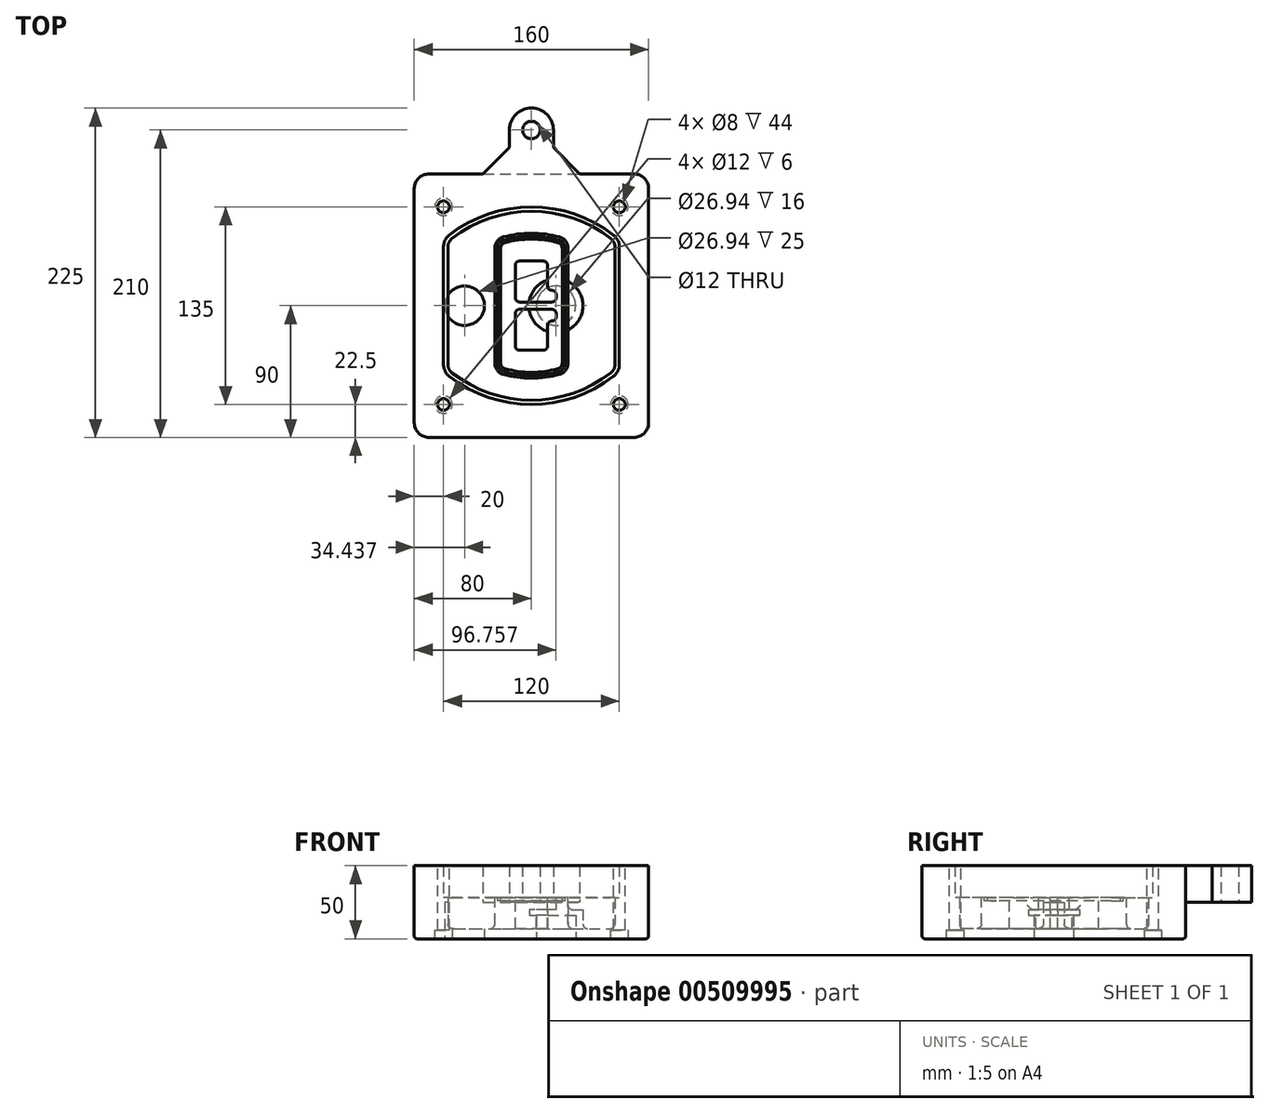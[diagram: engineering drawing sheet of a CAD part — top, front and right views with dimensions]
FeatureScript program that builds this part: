
annotation { "Feature Type Name" : "Feature", "Feature Type Description" : "" }
export const myFeature = defineFeature(function(context is Context, id is Id, definition is map)
    precondition{}
    {
        {
            var Q0;
            Q0=qCreatedBy(makeId("Top.planeOp"),FACE);
            var sketch = newSketch(context, id + "F0", { "sketchPlane" : qUnion([Q0])});
            skPoint(sketch, "E0.rect.middle", {"position": v(0, 0) * mm});
            skLineSegment(sketch, "E1.bottom", {"start": v(-70, -90) * mm, "end": v(70, -90) * mm});
            skLineSegment(sketch, "E1.top", {"start": v(-70, 90) * mm, "end": v(70, 90) * mm});
            skLineSegment(sketch, "E1.left", {"start": v(-80, -80) * mm, "end": v(-80, 80) * mm});
            skLineSegment(sketch, "E1.right", {"start": v(80, -80) * mm, "end": v(80, 80) * mm});
            skLineSegment(sketch, "E2", {"start": v(-80, 90) * mm, "end": v(80, -90) * mm, "construction": true});
            skLineSegment(sketch, "E3", {"start": v(80, 90) * mm, "end": v(-80, -90) * mm, "construction": true});
            skCircle(sketch, "E4", {"center": v(-60, 67.5) * mm, "radius": 4 * mm});
            skCircle(sketch, "E5", {"center": v(60, 67.5) * mm, "radius": 4 * mm});
            skCircle(sketch, "E6", {"center": v(60, -67.5) * mm, "radius": 4 * mm});
            skCircle(sketch, "E7", {"center": v(-60, -67.5) * mm, "radius": 4 * mm});
            skLineSegment(sketch, "E8", {"start": v(-60, 67.5) * mm, "end": v(60, 67.5) * mm, "construction": true});
            skLineSegment(sketch, "E9", {"start": v(60, 67.5) * mm, "end": v(60, -67.5) * mm, "construction": true});
            skLineSegment(sketch, "E10", {"start": v(60, -67.5) * mm, "end": v(-60, -67.5) * mm, "construction": true});
            skLineSegment(sketch, "E11", {"start": v(-60, -67.5) * mm, "end": v(-60, 67.5) * mm, "construction": true});
            skLineSegment(sketch, "E12", {"start": v(-60, 40.3) * mm, "end": v(-60, -40.3) * mm});
            skLineSegment(sketch, "E13", {"start": v(60, 40.3) * mm, "end": v(60, -40.3) * mm});
            skArc(sketch, "E14", {"start": v(56.15, 48.18) * mm, "mid": v(0, 67.5) * mm, "end": v(-56.15, 48.18) * mm});
            skArc(sketch, "E15", {"start": v(-56.15, -48.18) * mm, "mid": v(0, -67.5) * mm, "end": v(56.15, -48.18) * mm});
            skLineSegment(sketch, "E16", {"start": v(-60, 0) * mm, "end": v(60, 0) * mm, "construction": true});
            skPoint(sketch, "E17.visualSharp", {"position": v(-60, -45) * mm});
            skArc(sketch, "E17.filletArc", {"start": v(-60, -40.3) * mm, "mid": v(-58.99, -44.68) * mm, "end": v(-56.15, -48.18) * mm});
            skPoint(sketch, "E18.visualSharp", {"position": v(-60, 45) * mm});
            skArc(sketch, "E18.filletArc", {"start": v(-56.15, 48.18) * mm, "mid": v(-58.99, 44.68) * mm, "end": v(-60, 40.3) * mm});
            skPoint(sketch, "E19.visualSharp", {"position": v(60, 45) * mm});
            skArc(sketch, "E19.filletArc", {"start": v(60, 40.3) * mm, "mid": v(58.99, 44.68) * mm, "end": v(56.15, 48.18) * mm});
            skPoint(sketch, "E20.visualSharp", {"position": v(60, -45) * mm});
            skArc(sketch, "E20.filletArc", {"start": v(56.15, -48.18) * mm, "mid": v(58.99, -44.68) * mm, "end": v(60, -40.3) * mm});
            skPoint(sketch, "E21.visualSharp", {"position": v(-80, 90) * mm});
            skArc(sketch, "E21.filletArc", {"start": v(-70, 90) * mm, "mid": v(-77.07, 87.07) * mm, "end": v(-80, 80) * mm});
            skPoint(sketch, "E22.visualSharp", {"position": v(80, 90) * mm});
            skArc(sketch, "E22.filletArc", {"start": v(80, 80) * mm, "mid": v(77.07, 87.07) * mm, "end": v(70, 90) * mm});
            skPoint(sketch, "E23.visualSharp", {"position": v(80, -90) * mm});
            skArc(sketch, "E23.filletArc", {"start": v(70, -90) * mm, "mid": v(77.07, -87.07) * mm, "end": v(80, -80) * mm});
            skPoint(sketch, "E24.visualSharp", {"position": v(-80, -90) * mm});
            skArc(sketch, "E24.filletArc", {"start": v(-80, -80) * mm, "mid": v(-77.07, -87.07) * mm, "end": v(-70, -90) * mm});
            skArc(sketch, "E25.0", {"start": v(57, 40.3) * mm, "mid": v(56.3, 43.36) * mm, "end": v(54.3, 45.81) * mm});
            skLineSegment(sketch, "E25.1", {"start": v(57, 40.3) * mm, "end": v(57, -40.3) * mm});
            skArc(sketch, "E25.2", {"start": v(54.3, -45.81) * mm, "mid": v(56.3, -43.36) * mm, "end": v(57, -40.3) * mm});
            skArc(sketch, "E25.3", {"start": v(-54.3, -45.81) * mm, "mid": v(0, -64.5) * mm, "end": v(54.3, -45.81) * mm});
            skArc(sketch, "E25.4", {"start": v(-57, -40.3) * mm, "mid": v(-56.3, -43.36) * mm, "end": v(-54.3, -45.81) * mm});
            skArc(sketch, "E25.5", {"start": v(54.3, 45.81) * mm, "mid": v(0, 64.5) * mm, "end": v(-54.3, 45.81) * mm});
            skLineSegment(sketch, "E25.6", {"start": v(-57, 40.3) * mm, "end": v(-57, -40.3) * mm});
            skArc(sketch, "E25.7", {"start": v(-54.3, 45.81) * mm, "mid": v(-56.3, 43.36) * mm, "end": v(-57, 40.3) * mm});
            skArc(sketch, "E26.0", {"start": v(-58.62, 51.33) * mm, "mid": v(-62.58, 46.43) * mm, "end": v(-64, 40.3) * mm});
            skArc(sketch, "E26.1", {"start": v(58.62, 51.33) * mm, "mid": v(0, 71.5) * mm, "end": v(-58.62, 51.33) * mm});
            skArc(sketch, "E26.2", {"start": v(64, 40.3) * mm, "mid": v(62.58, 46.43) * mm, "end": v(58.62, 51.33) * mm});
            skLineSegment(sketch, "E26.3", {"start": v(64, 40.3) * mm, "end": v(64, -40.3) * mm});
            skArc(sketch, "E26.4", {"start": v(58.62, -51.33) * mm, "mid": v(62.58, -46.43) * mm, "end": v(64, -40.3) * mm});
            skLineSegment(sketch, "E26.5", {"start": v(-64, 40.3) * mm, "end": v(-64, -40.3) * mm});
            skArc(sketch, "E26.6", {"start": v(-58.62, -51.33) * mm, "mid": v(0, -71.5) * mm, "end": v(58.62, -51.33) * mm});
            skArc(sketch, "E26.7", {"start": v(-64, -40.3) * mm, "mid": v(-62.58, -46.43) * mm, "end": v(-58.62, -51.33) * mm});
            skSolve(sketch);
        }
        {
            var Q0;
            Q0=makeQuery(id+"F0.imprint","IMPRINT",FACE,{"disambiguationData":[TD([[makeQuery(id+"F0.imprint","IMPRINT",EDGE,{"derivedFrom":sQuery(id+"F0.wireOp",EDGE,"E1.bottom")}),1.0]])]});
            var Q1;
            Q1=makeQuery(id+"F0.imprint","IMPRINT",FACE,{"disambiguationData":[TD([[makeQuery(id+"F0.imprint","IMPRINT",EDGE,{"derivedFrom":sQuery(id+"F0.wireOp",EDGE,"E12")}),1.0]])]});
            var Q2;
            Q2=makeQuery(id+"F0.imprint","IMPRINT",FACE,{"disambiguationData":[TD([[makeQuery(id+"F0.imprint","IMPRINT",EDGE,{"derivedFrom":sQuery(id+"F0.wireOp",EDGE,"E25.0")}),1.0]])]});
            var Q3;
            Q3=makeQuery(id+"F0.imprint","IMPRINT",FACE,{"disambiguationData":[TD([[makeQuery(id+"F0.imprint","IMPRINT",EDGE,{"derivedFrom":sQuery(id+"F0.wireOp",EDGE,"E12")}),-1.0]])]});
            extrude(context, id + "F1", {"entities" : qUnion([Q0, Q1, Q2, Q3]), "oppositeDirection" : true, "depth" : 25 * mm});
        }
        {
            var Q0;
            Q0=makeQuery(id+"F0.imprint","IMPRINT",FACE,{"disambiguationData":[TD([[makeQuery(id+"F0.imprint","IMPRINT",EDGE,{"derivedFrom":sQuery(id+"F0.wireOp",EDGE,"E12")}),1.0]])]});
            extrude(context, id + "F2", {"entities" : qUnion([Q0]), "operationType" : NewBodyOperationType.ADD, "depth" : 3 * mm});
        }
        {
            var Q0;
            Q0=makeQuery(id+"F0.imprint","IMPRINT",FACE,{"disambiguationData":[TD([[makeQuery(id+"F0.imprint","IMPRINT",EDGE,{"derivedFrom":sQuery(id+"F0.wireOp",EDGE,"E25.0")}),1.0]])]});
            extrude(context, id + "F3", {"entities" : qUnion([Q0]), "operationType" : NewBodyOperationType.REMOVE, "oppositeDirection" : true, "depth" : 18 * mm});
        }
        {
            var Q0;
            Q0=makeQuery(id+"F2.opExtrude","CAP_FACE",FACE,{"disambiguationData":[OSD([sQuery(id+"F0.wireOp",EDGE,"E12"),sQuery(id+"F0.wireOp",EDGE,"E13"),sQuery(id+"F0.wireOp",EDGE,"E14"),sQuery(id+"F0.wireOp",EDGE,"E15"),sQuery(id+"F0.wireOp",EDGE,"E17.filletArc"),sQuery(id+"F0.wireOp",EDGE,"E18.filletArc"),sQuery(id+"F0.wireOp",EDGE,"E19.filletArc"),sQuery(id+"F0.wireOp",EDGE,"E20.filletArc"),sQuery(id+"F0.wireOp",EDGE,"E25.0"),sQuery(id+"F0.wireOp",EDGE,"E25.1"),sQuery(id+"F0.wireOp",EDGE,"E25.2"),sQuery(id+"F0.wireOp",EDGE,"E25.3"),sQuery(id+"F0.wireOp",EDGE,"E25.4"),sQuery(id+"F0.wireOp",EDGE,"E25.5"),sQuery(id+"F0.wireOp",EDGE,"E25.6"),sQuery(id+"F0.wireOp",EDGE,"E25.7")])],"isStart":false});
            var sketch = newSketch(context, id + "F4", { "sketchPlane" : qUnion([Q0])});
            skArc(sketch, "E27.0", {"start": v(-19.08, -46.97) * mm, "mid": v(0, -49.5) * mm, "end": v(19.08, -46.97) * mm});
            skArc(sketch, "E28.0", {"start": v(19.08, 46.97) * mm, "mid": v(0, 49.5) * mm, "end": v(-19.08, 46.97) * mm});
            skLineSegment(sketch, "E29", {"start": v(-25, 39.25) * mm, "end": v(-25, -39.25) * mm});
            skLineSegment(sketch, "E30", {"start": v(25, 39.25) * mm, "end": v(25, -39.25) * mm});
            skLineSegment(sketch, "E31", {"start": v(-25, 45.1) * mm, "end": v(25, 45.1) * mm, "construction": true});
            skLineSegment(sketch, "E32", {"start": v(-25, -45.1) * mm, "end": v(25, -45.1) * mm, "construction": true});
            skPoint(sketch, "E33.visualSharp", {"position": v(-25, 45.1) * mm});
            skArc(sketch, "E33.filletArc", {"start": v(-19.08, 46.97) * mm, "mid": v(-23.35, 44.11) * mm, "end": v(-25, 39.25) * mm});
            skPoint(sketch, "E34.visualSharp", {"position": v(25, 45.1) * mm});
            skArc(sketch, "E34.filletArc", {"start": v(25, 39.25) * mm, "mid": v(23.35, 44.11) * mm, "end": v(19.08, 46.97) * mm});
            skPoint(sketch, "E35.visualSharp", {"position": v(25, -45.1) * mm});
            skArc(sketch, "E35.filletArc", {"start": v(19.08, -46.97) * mm, "mid": v(23.35, -44.11) * mm, "end": v(25, -39.25) * mm});
            skPoint(sketch, "E36.visualSharp", {"position": v(-25, -45.1) * mm});
            skArc(sketch, "E36.filletArc", {"start": v(-25, -39.25) * mm, "mid": v(-23.35, -44.11) * mm, "end": v(-19.08, -46.97) * mm});
            skArc(sketch, "E37.0", {"start": v(54.3, 45.81) * mm, "mid": v(0, 64.5) * mm, "end": v(-54.3, 45.81) * mm});
            skArc(sketch, "E37.1", {"start": v(-54.3, 45.81) * mm, "mid": v(-56.3, 43.36) * mm, "end": v(-57, 40.3) * mm});
            skLineSegment(sketch, "E37.2", {"start": v(-57, 40.3) * mm, "end": v(-57, -40.3) * mm});
            skArc(sketch, "E37.3", {"start": v(-57, -40.3) * mm, "mid": v(-56.3, -43.36) * mm, "end": v(-54.3, -45.81) * mm});
            skArc(sketch, "E37.4", {"start": v(-54.3, -45.81) * mm, "mid": v(0, -64.5) * mm, "end": v(54.3, -45.81) * mm});
            skArc(sketch, "E37.5", {"start": v(54.3, -45.81) * mm, "mid": v(56.3, -43.36) * mm, "end": v(57, -40.3) * mm});
            skLineSegment(sketch, "E37.6", {"start": v(57, 40.3) * mm, "end": v(57, -40.3) * mm});
            skArc(sketch, "E37.7", {"start": v(57, 40.3) * mm, "mid": v(56.3, 43.36) * mm, "end": v(54.3, 45.81) * mm});
            skLineSegment(sketch, "E38.0", {"start": v(23, 39.25) * mm, "end": v(23, -39.25) * mm});
            skArc(sketch, "E38.1", {"start": v(18.56, -45.04) * mm, "mid": v(21.76, -42.9) * mm, "end": v(23, -39.25) * mm});
            skArc(sketch, "E38.2", {"start": v(-18.56, -45.04) * mm, "mid": v(0, -47.5) * mm, "end": v(18.56, -45.04) * mm});
            skArc(sketch, "E38.3", {"start": v(-23, -39.25) * mm, "mid": v(-21.76, -42.9) * mm, "end": v(-18.56, -45.04) * mm});
            skLineSegment(sketch, "E38.4", {"start": v(-23, 39.25) * mm, "end": v(-23, -39.25) * mm});
            skArc(sketch, "E38.5", {"start": v(23, 39.25) * mm, "mid": v(21.76, 42.9) * mm, "end": v(18.56, 45.04) * mm});
            skArc(sketch, "E38.6", {"start": v(-18.56, 45.04) * mm, "mid": v(-21.76, 42.9) * mm, "end": v(-23, 39.25) * mm});
            skArc(sketch, "E38.7", {"start": v(18.56, 45.04) * mm, "mid": v(0, 47.5) * mm, "end": v(-18.56, 45.04) * mm});
            skArc(sketch, "E39.0", {"start": v(21, 39.25) * mm, "mid": v(20.18, 41.68) * mm, "end": v(18.04, 43.1) * mm});
            skLineSegment(sketch, "E39.1", {"start": v(21, 39.25) * mm, "end": v(21, -39.25) * mm});
            skArc(sketch, "E39.2", {"start": v(18.04, -43.1) * mm, "mid": v(20.18, -41.68) * mm, "end": v(21, -39.25) * mm});
            skArc(sketch, "E39.3", {"start": v(-18.04, -43.1) * mm, "mid": v(0, -45.5) * mm, "end": v(18.04, -43.1) * mm});
            skArc(sketch, "E39.4", {"start": v(-21, -39.25) * mm, "mid": v(-20.18, -41.68) * mm, "end": v(-18.04, -43.1) * mm});
            skArc(sketch, "E39.5", {"start": v(18.04, 43.1) * mm, "mid": v(0, 45.5) * mm, "end": v(-18.04, 43.1) * mm});
            skLineSegment(sketch, "E39.6", {"start": v(-21, 39.25) * mm, "end": v(-21, -39.25) * mm});
            skArc(sketch, "E39.7", {"start": v(-18.04, 43.1) * mm, "mid": v(-20.18, 41.68) * mm, "end": v(-21, 39.25) * mm});
            skLineSegment(sketch, "E40", {"start": v(-25, 0) * mm, "end": v(25, 0) * mm, "construction": true});
            skLineSegment(sketch, "E41", {"start": v(-11, 5.5) * mm, "end": v(-11, 27.5) * mm});
            skLineSegment(sketch, "E42", {"start": v(-8, 30.5) * mm, "end": v(8, 30.5) * mm});
            skLineSegment(sketch, "E43", {"start": v(11, 27.5) * mm, "end": v(11, 13.5) * mm});
            skLineSegment(sketch, "E44", {"start": v(14, 10.5) * mm, "end": v(14, 10.5) * mm});
            skLineSegment(sketch, "E45", {"start": v(17, 7.5) * mm, "end": v(17, 5.5) * mm});
            skLineSegment(sketch, "E46", {"start": v(14, 2.5) * mm, "end": v(-8, 2.5) * mm});
            skPoint(sketch, "E47.visualSharp", {"position": v(-11, 30.5) * mm});
            skArc(sketch, "E47.filletArc", {"start": v(-8, 30.5) * mm, "mid": v(-10.12, 29.62) * mm, "end": v(-11, 27.5) * mm});
            skPoint(sketch, "E48.visualSharp", {"position": v(11, 30.5) * mm});
            skArc(sketch, "E48.filletArc", {"start": v(11, 27.5) * mm, "mid": v(10.12, 29.62) * mm, "end": v(8, 30.5) * mm});
            skPoint(sketch, "E49.visualSharp", {"position": v(11, 10.5) * mm});
            skArc(sketch, "E49.filletArc", {"start": v(11, 13.5) * mm, "mid": v(11.88, 11.38) * mm, "end": v(14, 10.5) * mm});
            skPoint(sketch, "E50.visualSharp", {"position": v(17, 10.5) * mm});
            skArc(sketch, "E50.filletArc", {"start": v(17, 7.5) * mm, "mid": v(16.12, 9.62) * mm, "end": v(14, 10.5) * mm});
            skPoint(sketch, "E51.visualSharp", {"position": v(17, 2.5) * mm});
            skArc(sketch, "E51.filletArc", {"start": v(14, 2.5) * mm, "mid": v(16.12, 3.38) * mm, "end": v(17, 5.5) * mm});
            skPoint(sketch, "E52.visualSharp", {"position": v(-11, 2.5) * mm});
            skArc(sketch, "E52.filletArc", {"start": v(-11, 5.5) * mm, "mid": v(-10.12, 3.38) * mm, "end": v(-8, 2.5) * mm});
            skLineSegment(sketch, "E53.0.MirrorCS", {"start": v(14, -2.5) * mm, "end": v(-8, -2.5) * mm});
            skArc(sketch, "E54.0.MirrorCS", {"start": v(-11, -5.5) * mm, "mid": v(-10.12, -3.38) * mm, "end": v(-8, -2.5) * mm});
            skLineSegment(sketch, "E55.0.MirrorCS", {"start": v(-11, -5.5) * mm, "end": v(-11, -27.5) * mm});
            skArc(sketch, "E56.0.MirrorCS", {"start": v(-8, -30.5) * mm, "mid": v(-10.12, -29.62) * mm, "end": v(-11, -27.5) * mm});
            skLineSegment(sketch, "E57.0.MirrorCS", {"start": v(-8, -30.5) * mm, "end": v(8, -30.5) * mm});
            skArc(sketch, "E58.0.MirrorCS", {"start": v(11, -27.5) * mm, "mid": v(10.12, -29.62) * mm, "end": v(8, -30.5) * mm});
            skLineSegment(sketch, "E59.0.MirrorCS", {"start": v(11, -27.5) * mm, "end": v(11, -13.5) * mm});
            skArc(sketch, "E60.0.MirrorCS", {"start": v(11, -13.5) * mm, "mid": v(11.88, -11.38) * mm, "end": v(14, -10.5) * mm});
            skArc(sketch, "E61.0.MirrorCS", {"start": v(17, -7.5) * mm, "mid": v(16.12, -9.62) * mm, "end": v(14, -10.5) * mm});
            skLineSegment(sketch, "E62.0.MirrorCS", {"start": v(17, -7.5) * mm, "end": v(17, -5.5) * mm});
            skArc(sketch, "E63.0.MirrorCS", {"start": v(14, -2.5) * mm, "mid": v(16.12, -3.38) * mm, "end": v(17, -5.5) * mm});
            skSolve(sketch);
        }
        {
            var Q0;
            Q0=makeQuery(id+"F4.imprint","IMPRINT",FACE,{"disambiguationData":[TD([[makeQuery(id+"F4.imprint","IMPRINT",EDGE,{"derivedFrom":sQuery(id+"F4.wireOp",EDGE,"E27.0")}),1.0]])]});
            var Q1;
            Q1=makeQuery(id+"F4.imprint","IMPRINT",FACE,{"disambiguationData":[TD([[makeQuery(id+"F4.imprint","IMPRINT",EDGE,{"derivedFrom":sQuery(id+"F4.wireOp",EDGE,"E38.0")}),-1.0]])]});
            var Q2;
            Q2=makeQuery(id+"F4.imprint","IMPRINT",FACE,{"disambiguationData":[TD([[makeQuery(id+"F4.imprint","IMPRINT",EDGE,{"derivedFrom":sQuery(id+"F4.wireOp",EDGE,"E39.0")}),1.0]])]});
            extrude(context, id + "F5", {"entities" : qUnion([Q0, Q1, Q2]), "operationType" : NewBodyOperationType.ADD, "endBound" : BoundingType.UP_TO_NEXT, "oppositeDirection" : true, "depth" : 25 * mm});
        }
        {
            var Q0;
            Q0=makeQuery(id+"F4.imprint","IMPRINT",FACE,{"disambiguationData":[TD([[makeQuery(id+"F4.imprint","IMPRINT",EDGE,{"derivedFrom":sQuery(id+"F4.wireOp",EDGE,"E38.0")}),-1.0]])]});
            extrude(context, id + "F6", {"entities" : qUnion([Q0]), "operationType" : NewBodyOperationType.REMOVE, "oppositeDirection" : true, "depth" : 2 * mm});
        }
        {
            var Q0;
            Q0=makeQuery(id+"F1.opExtrude","CAP_FACE",FACE,{"disambiguationData":[OSD([sQuery(id+"F0.wireOp",EDGE,"E1.bottom"),sQuery(id+"F0.wireOp",EDGE,"E1.top"),sQuery(id+"F0.wireOp",EDGE,"E1.left"),sQuery(id+"F0.wireOp",EDGE,"E1.right"),sQuery(id+"F0.wireOp",EDGE,"E4"),sQuery(id+"F0.wireOp",EDGE,"E5"),sQuery(id+"F0.wireOp",EDGE,"E6"),sQuery(id+"F0.wireOp",EDGE,"E7"),sQuery(id+"F0.wireOp",EDGE,"E21.filletArc"),sQuery(id+"F0.wireOp",EDGE,"E22.filletArc"),sQuery(id+"F0.wireOp",EDGE,"E23.filletArc"),sQuery(id+"F0.wireOp",EDGE,"E24.filletArc")])],"isStart":false});
            var sketch = newSketch(context, id + "F7", { "sketchPlane" : qUnion([Q0])});
            skCircle(sketch, "E64", {"center": v(16.76, 0) * mm, "radius": 13.47 * mm});
            skCircle(sketch, "E65", {"center": v(-45.56, 0) * mm, "radius": 13.47 * mm});
            skLineSegment(sketch, "E66", {"start": v(80, 0) * mm, "end": v(-80, 0) * mm});
            skCircle(sketch, "E67", {"center": v(16.76, 0) * mm, "radius": 18.47 * mm});
            skCircle(sketch, "E68", {"center": v(60, -67.5) * mm, "radius": 6 * mm});
            skCircle(sketch, "E69", {"center": v(-60, -67.5) * mm, "radius": 6 * mm});
            skCircle(sketch, "E70", {"center": v(-60, 67.5) * mm, "radius": 6 * mm});
            skCircle(sketch, "E71", {"center": v(60, 67.5) * mm, "radius": 6 * mm});
            skSolve(sketch);
        }
        {
            var Q0;
            {var subQ1=sQuery(id+"F7.wireOp",EDGE,"E66");var subQ4=sQuery(id+"F7.wireOp",EDGE,"E64");var subQ6=makeQuery(id+"F7.imprint","INTERSECT",VERTEX,{"disambiguationData":[OD(0.0)],"derivedFrom":[subQ4,subQ1]});Q0=makeQuery(id+"F7.imprint","IMPRINT",FACE,{"disambiguationData":[TD([[makeQuery(id+"F7.imprint","IMPRINT",EDGE,{"disambiguationData":[TD([[subQ6,-1.0]])],"derivedFrom":subQ4}),-1.0]])]});}
            var Q1;
            {var subQ0=sQuery(id+"F7.wireOp",EDGE,"E66");var subQ1=sQuery(id+"F7.wireOp",EDGE,"E64");var subQ3=makeQuery(id+"F7.imprint","INTERSECT",VERTEX,{"disambiguationData":[OD(0.0)],"derivedFrom":[subQ1,subQ0]});Q1=makeQuery(id+"F7.imprint","IMPRINT",FACE,{"disambiguationData":[TD([[makeQuery(id+"F7.imprint","IMPRINT",EDGE,{"disambiguationData":[TD([[subQ3,-1.0]])],"derivedFrom":subQ1}),1.0]])]});}
            var Q2;
            {var subQ0=sQuery(id+"F7.wireOp",EDGE,"E66");var subQ1=sQuery(id+"F7.wireOp",EDGE,"E64");var subQ3=makeQuery(id+"F7.imprint","INTERSECT",VERTEX,{"disambiguationData":[OD(0.0)],"derivedFrom":[subQ1,subQ0]});Q2=makeQuery(id+"F7.imprint","IMPRINT",FACE,{"disambiguationData":[TD([[makeQuery(id+"F7.imprint","IMPRINT",EDGE,{"disambiguationData":[TD([[subQ3,1.0]])],"derivedFrom":subQ1}),1.0]])]});}
            var Q3;
            {var subQ1=sQuery(id+"F7.wireOp",EDGE,"E66");var subQ4=sQuery(id+"F7.wireOp",EDGE,"E64");var subQ6=makeQuery(id+"F7.imprint","INTERSECT",VERTEX,{"disambiguationData":[OD(0.0)],"derivedFrom":[subQ4,subQ1]});Q3=makeQuery(id+"F7.imprint","IMPRINT",FACE,{"disambiguationData":[TD([[makeQuery(id+"F7.imprint","IMPRINT",EDGE,{"disambiguationData":[TD([[subQ6,1.0]])],"derivedFrom":subQ4}),-1.0]])]});}
            extrude(context, id + "F8", {"entities" : qUnion([Q0, Q1, Q2, Q3]), "operationType" : NewBodyOperationType.ADD, "oppositeDirection" : true, "depth" : 20 * mm});
        }
        {
            var Q0;
            {var subQ0=sQuery(id+"F7.wireOp",EDGE,"E66");var subQ1=sQuery(id+"F7.wireOp",EDGE,"E64");var subQ3=makeQuery(id+"F7.imprint","INTERSECT",VERTEX,{"disambiguationData":[OD(0.0)],"derivedFrom":[subQ1,subQ0]});Q0=makeQuery(id+"F7.imprint","IMPRINT",FACE,{"disambiguationData":[TD([[makeQuery(id+"F7.imprint","IMPRINT",EDGE,{"disambiguationData":[TD([[subQ3,-1.0]])],"derivedFrom":subQ1}),1.0]])]});}
            var Q1;
            {var subQ0=sQuery(id+"F7.wireOp",EDGE,"E66");var subQ1=sQuery(id+"F7.wireOp",EDGE,"E64");var subQ3=makeQuery(id+"F7.imprint","INTERSECT",VERTEX,{"disambiguationData":[OD(0.0)],"derivedFrom":[subQ1,subQ0]});Q1=makeQuery(id+"F7.imprint","IMPRINT",FACE,{"disambiguationData":[TD([[makeQuery(id+"F7.imprint","IMPRINT",EDGE,{"disambiguationData":[TD([[subQ3,1.0]])],"derivedFrom":subQ1}),1.0]])]});}
            extrude(context, id + "F9", {"entities" : qUnion([Q0, Q1]), "operationType" : NewBodyOperationType.REMOVE, "oppositeDirection" : true, "depth" : 16 * mm});
        }
        {
            var Q0;
            {var subQ0=sQuery(id+"F7.wireOp",EDGE,"E66");var subQ1=sQuery(id+"F7.wireOp",EDGE,"E65");var subQ3=makeQuery(id+"F7.imprint","INTERSECT",VERTEX,{"disambiguationData":[OD(0.0)],"derivedFrom":[subQ1,subQ0]});Q0=makeQuery(id+"F7.imprint","IMPRINT",FACE,{"disambiguationData":[TD([[makeQuery(id+"F7.imprint","IMPRINT",EDGE,{"disambiguationData":[TD([[subQ3,-1.0]])],"derivedFrom":subQ1}),1.0]])]});}
            var Q1;
            {var subQ0=sQuery(id+"F7.wireOp",EDGE,"E66");var subQ1=sQuery(id+"F7.wireOp",EDGE,"E65");var subQ3=makeQuery(id+"F7.imprint","INTERSECT",VERTEX,{"disambiguationData":[OD(0.0)],"derivedFrom":[subQ1,subQ0]});Q1=makeQuery(id+"F7.imprint","IMPRINT",FACE,{"disambiguationData":[TD([[makeQuery(id+"F7.imprint","IMPRINT",EDGE,{"disambiguationData":[TD([[subQ3,1.0]])],"derivedFrom":subQ1}),1.0]])]});}
            extrude(context, id + "F10", {"entities" : qUnion([Q0, Q1]), "operationType" : NewBodyOperationType.REMOVE, "oppositeDirection" : true, "depth" : 25 * mm});
        }
        {
            var Q0;
            Q0=makeQuery(id+"F7.imprint","IMPRINT",FACE,{"disambiguationData":[TD([[makeQuery(id+"F7.imprint","IMPRINT",EDGE,{"derivedFrom":sQuery(id+"F7.wireOp",EDGE,"E68")}),1.0]])]});
            var Q1;
            Q1=makeQuery(id+"F7.imprint","IMPRINT",FACE,{"disambiguationData":[TD([[makeQuery(id+"F7.imprint","IMPRINT",EDGE,{"derivedFrom":makeQuery(id+"F1.opExtrude","CAP_EDGE",EDGE,{"disambiguationData":[OSD([sQuery(id+"F0.wireOp",EDGE,"E5")])],"isStart":false})}),-1.0]])]});
            var Q2;
            Q2=makeQuery(id+"F7.imprint","IMPRINT",FACE,{"disambiguationData":[TD([[makeQuery(id+"F7.imprint","IMPRINT",EDGE,{"derivedFrom":sQuery(id+"F7.wireOp",EDGE,"E69")}),1.0]])]});
            var Q3;
            Q3=makeQuery(id+"F7.imprint","IMPRINT",FACE,{"disambiguationData":[TD([[makeQuery(id+"F7.imprint","IMPRINT",EDGE,{"derivedFrom":makeQuery(id+"F1.opExtrude","CAP_EDGE",EDGE,{"disambiguationData":[OSD([sQuery(id+"F0.wireOp",EDGE,"E4")])],"isStart":false})}),-1.0]])]});
            var Q4;
            Q4=makeQuery(id+"F7.imprint","IMPRINT",FACE,{"disambiguationData":[TD([[makeQuery(id+"F7.imprint","IMPRINT",EDGE,{"derivedFrom":sQuery(id+"F7.wireOp",EDGE,"E70")}),1.0]])]});
            var Q5;
            Q5=makeQuery(id+"F7.imprint","IMPRINT",FACE,{"disambiguationData":[TD([[makeQuery(id+"F7.imprint","IMPRINT",EDGE,{"derivedFrom":makeQuery(id+"F1.opExtrude","CAP_EDGE",EDGE,{"disambiguationData":[OSD([sQuery(id+"F0.wireOp",EDGE,"E7")])],"isStart":false})}),-1.0]])]});
            var Q6;
            Q6=makeQuery(id+"F7.imprint","IMPRINT",FACE,{"disambiguationData":[TD([[makeQuery(id+"F7.imprint","IMPRINT",EDGE,{"derivedFrom":sQuery(id+"F7.wireOp",EDGE,"E71")}),1.0]])]});
            var Q7;
            Q7=makeQuery(id+"F7.imprint","IMPRINT",FACE,{"disambiguationData":[TD([[makeQuery(id+"F7.imprint","IMPRINT",EDGE,{"derivedFrom":makeQuery(id+"F1.opExtrude","CAP_EDGE",EDGE,{"disambiguationData":[OSD([sQuery(id+"F0.wireOp",EDGE,"E6")])],"isStart":false})}),-1.0]])]});
            extrude(context, id + "F11", {"entities" : qUnion([Q0, Q1, Q2, Q3, Q4, Q5, Q6, Q7]), "operationType" : NewBodyOperationType.REMOVE, "oppositeDirection" : true, "depth" : 6 * mm});
        }
        {
            var Q0;
            Q0=makeQuery(id+"F9.boolean.opBoolean","COPY",FACE,{"derivedFrom":makeQuery(id+"F9.opExtrude","CAP_FACE",FACE,{"disambiguationData":[OSD([sQuery(id+"F7.wireOp",EDGE,"E64")])],"isStart":false})});
            var sketch = newSketch(context, id + "F12", { "sketchPlane" : qUnion([Q0])});
            skArc(sketch, "E72.0", {"start": v(11, 17.55) * mm, "mid": v(2.57, 11.82) * mm, "end": v(-1.54, 2.5) * mm});
            skArc(sketch, "E72.1", {"start": v(-1.54, -2.5) * mm, "mid": v(2.57, -11.82) * mm, "end": v(11, -17.55) * mm});
            skLineSegment(sketch, "E73", {"start": v(-1.54, -2.5) * mm, "end": v(14, -2.5) * mm});
            skLineSegment(sketch, "E74.0", {"start": v(14, 2.5) * mm, "end": v(-1.54, 2.5) * mm});
            skArc(sketch, "E74.1", {"start": v(14, 2.5) * mm, "mid": v(16.12, 3.38) * mm, "end": v(17, 5.5) * mm});
            skLineSegment(sketch, "E74.2", {"start": v(17, 7.5) * mm, "end": v(17, 5.5) * mm});
            skArc(sketch, "E74.3", {"start": v(17, 7.5) * mm, "mid": v(16.12, 9.62) * mm, "end": v(14, 10.5) * mm});
            skArc(sketch, "E74.4", {"start": v(11, 13.5) * mm, "mid": v(11.88, 11.38) * mm, "end": v(14, 10.5) * mm});
            skLineSegment(sketch, "E74.5", {"start": v(11, 17.55) * mm, "end": v(11, 13.5) * mm});
            skLineSegment(sketch, "E74.7", {"start": v(14, -2.5) * mm, "end": v(-1.54, -2.5) * mm});
            skArc(sketch, "E74.8", {"start": v(14, -2.5) * mm, "mid": v(16.12, -3.38) * mm, "end": v(17, -5.5) * mm});
            skLineSegment(sketch, "E74.9", {"start": v(17, -7.5) * mm, "end": v(17, -5.5) * mm});
            skArc(sketch, "E74.10", {"start": v(17, -7.5) * mm, "mid": v(16.12, -9.62) * mm, "end": v(14, -10.5) * mm});
            skArc(sketch, "E74.11", {"start": v(11, -13.5) * mm, "mid": v(11.88, -11.38) * mm, "end": v(14, -10.5) * mm});
            skLineSegment(sketch, "E74.12", {"start": v(11, -17.55) * mm, "end": v(11, -13.5) * mm});
            skPoint(sketch, "E75.orphan", {"position": v(11, -27.5) * mm});
            skPoint(sketch, "E76.orphan", {"position": v(-8, -2.5) * mm});
            skPoint(sketch, "E77.orphan", {"position": v(-8, 2.5) * mm});
            skPoint(sketch, "E78.orphan", {"position": v(11, 27.5) * mm});
            skSolve(sketch);
        }
        {
            var Q0;
            {var subQ7=sQuery(id+"F12.wireOp",EDGE,"E72.0");var subQ14=sQuery(id+"F12.wireOp",EDGE,"E72.1");var subQ16=sQuery(id+"F12.wireOp",EDGE,"E74.1");var subQ18=sQuery(id+"F12.wireOp",EDGE,"E74.8");Q0=qUnion([makeQuery(id+"F12.imprint","IMPRINT",FACE,{"disambiguationData":[TD([[makeQuery(id+"F12.imprint","IMPRINT",EDGE,{"derivedFrom":subQ7}),1.0]])]}),makeQuery(id+"F12.imprint","IMPRINT",FACE,{"disambiguationData":[TD([[makeQuery(id+"F12.imprint","IMPRINT",EDGE,{"derivedFrom":subQ14}),1.0]])]}),makeQuery(id+"F12.imprint","IMPRINT",FACE,{"disambiguationData":[TD([[makeQuery(id+"F12.imprint","IMPRINT",EDGE,{"derivedFrom":subQ16}),1.0]])]}),makeQuery(id+"F12.imprint","IMPRINT",FACE,{"disambiguationData":[TD([[makeQuery(id+"F12.imprint","IMPRINT",EDGE,{"derivedFrom":subQ18}),-1.0]])]})]);}
            var Q1;
            Q1=makeQuery(id+"F5.boolean.opBoolean","SPLIT",FACE,{"disambiguationData":[TD([makeQuery(id+"F5.opExtrude","SWEPT_FACE",FACE,{"disambiguationData":[OSD([sQuery(id+"F4.wireOp",EDGE,"E41")])]})])],"derivedFrom":makeQuery(id+"F3.boolean.opBoolean","COPY",FACE,{"derivedFrom":makeQuery(id+"F3.opExtrude","CAP_FACE",FACE,{"disambiguationData":[OSD([sQuery(id+"F0.wireOp",EDGE,"E25.0"),sQuery(id+"F0.wireOp",EDGE,"E25.1"),sQuery(id+"F0.wireOp",EDGE,"E25.2"),sQuery(id+"F0.wireOp",EDGE,"E25.3"),sQuery(id+"F0.wireOp",EDGE,"E25.4"),sQuery(id+"F0.wireOp",EDGE,"E25.5"),sQuery(id+"F0.wireOp",EDGE,"E25.6"),sQuery(id+"F0.wireOp",EDGE,"E25.7")])],"isStart":false})})});
            extrude(context, id + "F13", {"entities" : qUnion([Q0]), "operationType" : NewBodyOperationType.REMOVE, "endBound" : BoundingType.UP_TO_SURFACE, "endBoundEntityFace" : qUnion([Q1]), "depth" : 25 * mm});
        }
        {
            var Q0;
            Q0=makeQuery(id+"F3.boolean.opBoolean","COPY",EDGE,{"derivedFrom":makeQuery(id+"F3.opExtrude","CAP_EDGE",EDGE,{"disambiguationData":[OSD([sQuery(id+"F0.wireOp",EDGE,"E25.6")])],"isStart":false})});
            var Q1;
            Q1=makeQuery(id+"F8.boolean.opBoolean","INTERSECT",EDGE,{"derivedFrom":[makeQuery(id+"F5.opExtrude","SWEPT_FACE",FACE,{"disambiguationData":[OSD([sQuery(id+"F4.wireOp",EDGE,"E30")])]}),makeQuery(id+"F8.opExtrude","CAP_FACE",FACE,{"disambiguationData":[OSD([sQuery(id+"F7.wireOp",EDGE,"E67")])],"isStart":false})]});
            var Q2;
            Q2=makeQuery(id+"F8.boolean.opBoolean","INTERSECT",EDGE,{"disambiguationData":[OD(1.0)],"derivedFrom":[makeQuery(id+"F5.opExtrude","SWEPT_FACE",FACE,{"disambiguationData":[OSD([sQuery(id+"F4.wireOp",EDGE,"E30")])]}),makeQuery(id+"F8.opExtrude","SWEPT_FACE",FACE,{"disambiguationData":[OSD([sQuery(id+"F7.wireOp",EDGE,"E67")])]})]});
            var Q3;
            {var subQ0=sQuery(id+"F4.wireOp",EDGE,"E30");Q3=makeQuery(id+"F8.boolean.opBoolean","SPLIT",EDGE,{"disambiguationData":[TD([makeQuery(id+"F5.opExtrude","SWEPT_FACE",FACE,{"disambiguationData":[OSD([sQuery(id+"F4.wireOp",EDGE,"E35.filletArc")])]})])],"derivedFrom":makeQuery(id+"F5.opExtrude","CAP_EDGE",EDGE,{"disambiguationData":[OSD([subQ0])],"isStart":false})});}
            var Q4;
            {var subQ0=sQuery(id+"F0.wireOp",EDGE,"E25.7");var subQ1=sQuery(id+"F0.wireOp",EDGE,"E25.1");var subQ2=sQuery(id+"F0.wireOp",EDGE,"E25.6");var subQ3=sQuery(id+"F0.wireOp",EDGE,"E25.5");var subQ4=sQuery(id+"F0.wireOp",EDGE,"E25.4");var subQ5=sQuery(id+"F0.wireOp",EDGE,"E25.0");var subQ6=sQuery(id+"F0.wireOp",EDGE,"E25.2");var subQ7=sQuery(id+"F0.wireOp",EDGE,"E25.3");Q4=makeQuery(id+"F8.boolean.opBoolean","INTERSECT",EDGE,{"derivedFrom":[makeQuery(id+"F5.boolean.opBoolean","SPLIT",FACE,{"disambiguationData":[TD([makeQuery(id+"F2.opExtrude","SWEPT_FACE",FACE,{"disambiguationData":[OSD([subQ5])]})])],"derivedFrom":makeQuery(id+"F3.boolean.opBoolean","COPY",FACE,{"derivedFrom":makeQuery(id+"F3.opExtrude","CAP_FACE",FACE,{"disambiguationData":[OSD([subQ5,subQ1,subQ6,subQ7,subQ4,subQ3,subQ2,subQ0])],"isStart":false})})}),makeQuery(id+"F8.opExtrude","SWEPT_FACE",FACE,{"disambiguationData":[OSD([sQuery(id+"F7.wireOp",EDGE,"E67")])]})]});}
            var Q5;
            Q5=makeQuery(id+"F8.boolean.opBoolean","INTERSECT",EDGE,{"disambiguationData":[OD(0.0)],"derivedFrom":[makeQuery(id+"F5.opExtrude","SWEPT_FACE",FACE,{"disambiguationData":[OSD([sQuery(id+"F4.wireOp",EDGE,"E30")])]}),makeQuery(id+"F8.opExtrude","SWEPT_FACE",FACE,{"disambiguationData":[OSD([sQuery(id+"F7.wireOp",EDGE,"E67")])]})]});
            fillet(context, id + "F14", {"entities" : qUnion([Q0, Q1, Q2, Q3, Q4, Q5]), "radius" : 3 * mm, "tangentPropagation" : true, "allowEdgeOverflow" : false});
        }
        {
            var Q0;
            Q0=makeQuery(id+"F1.opExtrude","CAP_EDGE",EDGE,{"disambiguationData":[OSD([sQuery(id+"F0.wireOp",EDGE,"E1.bottom")])],"isStart":false});
            fillet(context, id + "F15", {"entities" : qUnion([Q0]), "radius" : 2 * mm, "tangentPropagation" : true, "allowEdgeOverflow" : false});
        }
        {
            var Q0;
            {var subQ0=sQuery(id+"F0.wireOp",EDGE,"E21.filletArc");var subQ1=sQuery(id+"F0.wireOp",EDGE,"E7");var subQ2=sQuery(id+"F0.wireOp",EDGE,"E6");var subQ3=sQuery(id+"F0.wireOp",EDGE,"E5");var subQ4=sQuery(id+"F0.wireOp",EDGE,"E4");var subQ5=sQuery(id+"F0.wireOp",EDGE,"E22.filletArc");var subQ6=sQuery(id+"F0.wireOp",EDGE,"E1.bottom");var subQ7=sQuery(id+"F0.wireOp",EDGE,"E1.right");var subQ8=sQuery(id+"F0.wireOp",EDGE,"E1.top");var subQ9=sQuery(id+"F0.wireOp",EDGE,"E1.left");var subQ10=sQuery(id+"F0.wireOp",EDGE,"E23.filletArc");var subQ11=sQuery(id+"F0.wireOp",EDGE,"E24.filletArc");Q0=makeQuery(id+"F2.boolean.opBoolean","SPLIT",FACE,{"disambiguationData":[TD([makeQuery(id+"F1.opExtrude","SWEPT_FACE",FACE,{"disambiguationData":[OSD([subQ6])]})])],"derivedFrom":makeQuery(id+"F1.opExtrude","CAP_FACE",FACE,{"disambiguationData":[OSD([subQ6,subQ8,subQ9,subQ7,subQ4,subQ3,subQ2,subQ1,subQ0,subQ5,subQ10,subQ11])],"isStart":true})});}
            var sketch = newSketch(context, id + "F16", { "sketchPlane" : qUnion([Q0])});
            skLineSegment(sketch, "E79", {"start": v(0, 90) * mm, "end": v(0, 120) * mm, "construction": true});
            skCircle(sketch, "E80", {"center": v(0, 120) * mm, "radius": 6 * mm});
            skLineSegment(sketch, "E81", {"start": v(-33, 90) * mm, "end": v(-15, 108) * mm});
            skLineSegment(sketch, "E82", {"start": v(-15, 108) * mm, "end": v(-15, 120) * mm});
            skLineSegment(sketch, "E83", {"start": v(33, 90) * mm, "end": v(15, 108) * mm});
            skLineSegment(sketch, "E84", {"start": v(15, 108) * mm, "end": v(15, 120) * mm});
            skArc(sketch, "E85", {"start": v(15, 120) * mm, "mid": v(0, 135) * mm, "end": v(-15, 120) * mm});
            skLineSegment(sketch, "E86", {"start": v(-80, 0) * mm, "end": v(80, 0) * mm, "construction": true});
            skArc(sketch, "E87.MirrorCS", {"start": v(15, -120) * mm, "mid": v(0, -135) * mm, "end": v(-15, -120) * mm});
            skCircle(sketch, "E88.MirrorC", {"center": v(0, -120) * mm, "radius": 6 * mm});
            skLineSegment(sketch, "E89.MirrorCS", {"start": v(0, -90) * mm, "end": v(0, -120) * mm, "construction": true});
            skLineSegment(sketch, "E90.MirrorCS", {"start": v(-15, -108) * mm, "end": v(-15, -120) * mm});
            skLineSegment(sketch, "E91.MirrorCS", {"start": v(15, -108) * mm, "end": v(15, -120) * mm});
            skLineSegment(sketch, "E92.MirrorCS", {"start": v(33, -90) * mm, "end": v(15, -108) * mm});
            skLineSegment(sketch, "E93.MirrorCS", {"start": v(-33, -90) * mm, "end": v(-15, -108) * mm});
            skSolve(sketch);
        }
        {
            var Q0;
            Q0=qCreatedBy(makeId("Top.planeOp"),FACE);
            var sketch = newSketch(context, id + "F17", { "sketchPlane" : qUnion([Q0])});
            skSolve(sketch);
        }
        {
            var Q0;
            Q0 = qSketchRegion(id + "F17", true);
            var Q1;
            Q1=makeQuery(id+"F16.imprint","IMPRINT",FACE,{"disambiguationData":[TD([[makeQuery(id+"F16.imprint","IMPRINT",EDGE,{"derivedFrom":makeQuery(id+"F1.opExtrude","CAP_EDGE",EDGE,{"disambiguationData":[OSD([sQuery(id+"F0.wireOp",EDGE,"E1.left")])],"isStart":true})}),-1.0]])]});
            var Q2;
            Q2=makeQuery(id+"F16.imprint","IMPRINT",FACE,{"disambiguationData":[TD([[makeQuery(id+"F16.imprint","IMPRINT",EDGE,{"derivedFrom":sQuery(id+"F16.wireOp",EDGE,"E80")}),-1.0]])]});
            var Q3;
            Q3=makeQuery(id+"F16.imprint","IMPRINT",FACE,{"disambiguationData":[TD([[makeQuery(id+"F16.imprint","IMPRINT",EDGE,{"derivedFrom":sQuery(id+"F16.wireOp",EDGE,"E87.MirrorCS")}),-1.0]])]});
            extrude(context, id + "F18", {"entities" : qUnion([Q0, Q1, Q2, Q3]), "operationType" : NewBodyOperationType.ADD, "depth" : 25 * mm});
        }
    });
